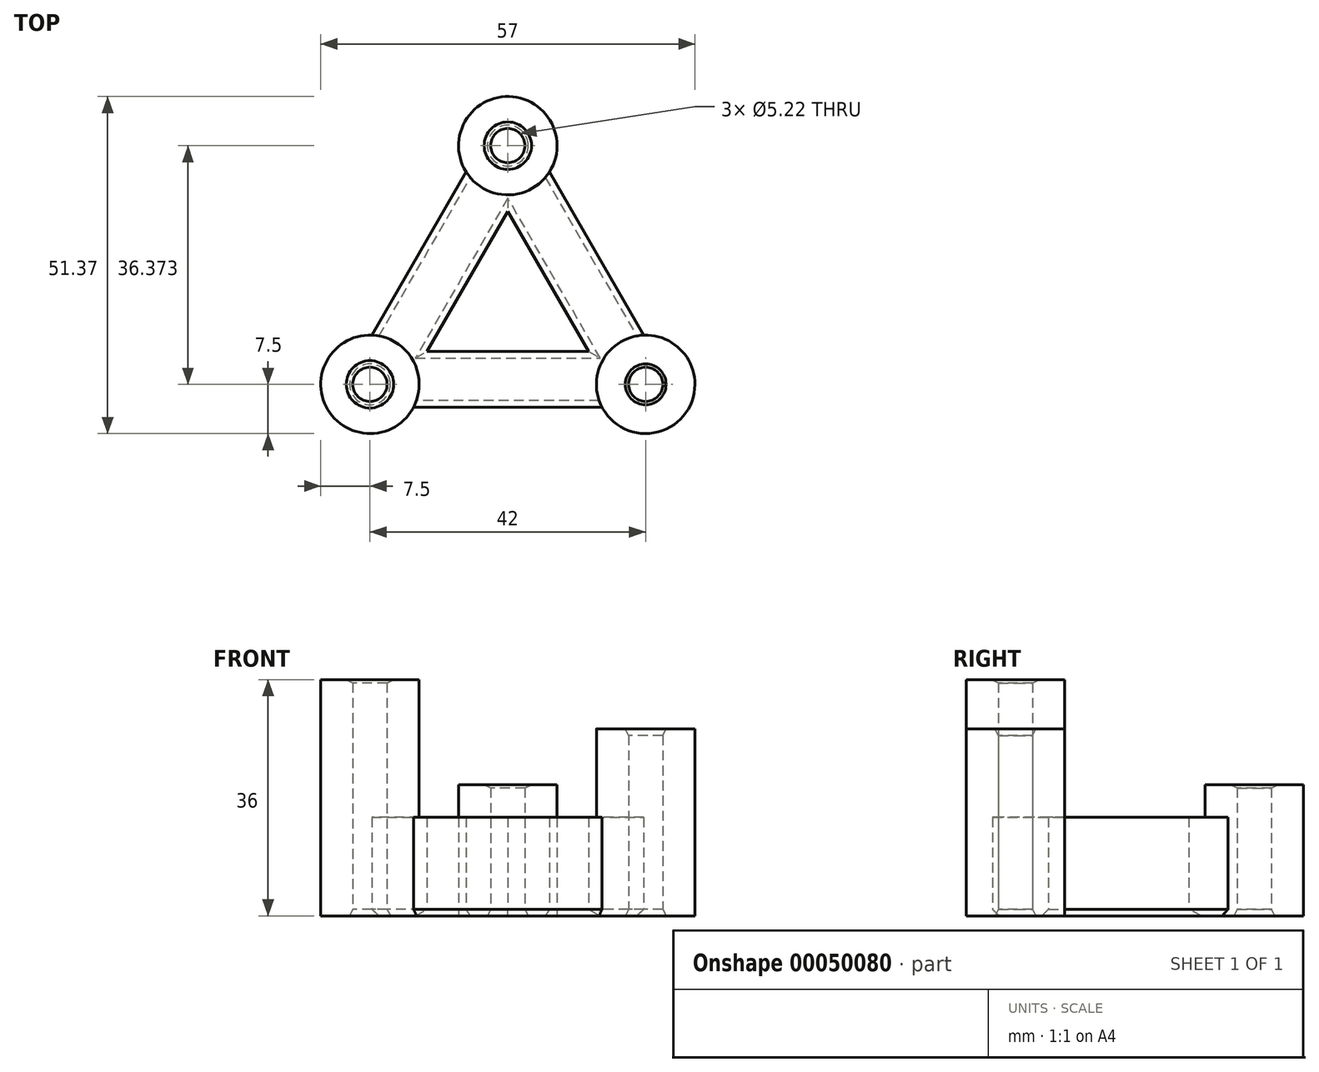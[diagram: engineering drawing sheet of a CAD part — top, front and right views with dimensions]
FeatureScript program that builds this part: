
annotation { "Feature Type Name" : "Feature", "Feature Type Description" : "" }
export const myFeature = defineFeature(function(context is Context, id is Id, definition is map)
    precondition{}
    {
        {
            var Q0;
            Q0=qCreatedBy(makeId("Top.planeOp"),FACE);
            var sketch = newSketch(context, id + "F0", { "sketchPlane" : qUnion([Q0])});
            skLineSegment(sketch, "E0", {"start": v(-21, 0) * mm, "end": v(21, 0) * mm, "construction": true});
            skLineSegment(sketch, "E1", {"start": v(21, 0) * mm, "end": v(0, 36.37) * mm, "construction": true});
            skLineSegment(sketch, "E2", {"start": v(0, 36.37) * mm, "end": v(-21, 0) * mm, "construction": true});
            skArc(sketch, "E3", {"start": v(6.35, 32.38) * mm, "mid": v(0, 43.87) * mm, "end": v(-6.35, 32.38) * mm});
            skArc(sketch, "E4", {"start": v(-20.71, 7.5) * mm, "mid": v(-27.5, -3.75) * mm, "end": v(-14.37, -3.5) * mm});
            skArc(sketch, "E5", {"start": v(14.37, -3.5) * mm, "mid": v(27.5, -3.75) * mm, "end": v(20.71, 7.5) * mm});
            skCircle(sketch, "E6", {"center": v(0, 36.37) * mm, "radius": 2.6 * mm});
            skCircle(sketch, "E7", {"center": v(21, 0) * mm, "radius": 2.6 * mm});
            skCircle(sketch, "E8", {"center": v(-21, 0) * mm, "radius": 2.6 * mm});
            skLineSegment(sketch, "E9", {"start": v(-20.71, 7.5) * mm, "end": v(-6.35, 32.38) * mm});
            skLineSegment(sketch, "E10", {"start": v(6.35, 32.38) * mm, "end": v(20.71, 7.5) * mm});
            skLineSegment(sketch, "E11", {"start": v(14.37, -3.5) * mm, "end": v(-14.37, -3.5) * mm});
            skLineSegment(sketch, "E12", {"start": v(-12.34, 5) * mm, "end": v(12.34, 5) * mm});
            skLineSegment(sketch, "E13", {"start": v(12.34, 5) * mm, "end": v(0, 26.37) * mm});
            skLineSegment(sketch, "E14", {"start": v(0, 26.37) * mm, "end": v(-12.34, 5) * mm});
            skSolve(sketch);
        }
        {
            var Q0;
            Q0=makeQuery(id+"F0.imprint","IMPRINT",FACE,{"disambiguationData":[TD([[makeQuery(id+"F0.imprint","IMPRINT",EDGE,{"derivedFrom":sQuery(id+"F0.wireOp",EDGE,"E3")}),1.0]])]});
            extrude(context, id + "F1", {"entities" : qUnion([Q0]), "depth" : 15 * mm, "offsetDistance" : 25 * mm});
        }
        {
            var Q0;
            Q0=makeQuery(id+"F1.opExtrude","CAP_FACE",FACE,{"disambiguationData":[OSD([sQuery(id+"F0.wireOp",EDGE,"E3"),sQuery(id+"F0.wireOp",EDGE,"E4"),sQuery(id+"F0.wireOp",EDGE,"E5"),sQuery(id+"F0.wireOp",EDGE,"E6"),sQuery(id+"F0.wireOp",EDGE,"E7"),sQuery(id+"F0.wireOp",EDGE,"E8"),sQuery(id+"F0.wireOp",EDGE,"E9"),sQuery(id+"F0.wireOp",EDGE,"E10"),sQuery(id+"F0.wireOp",EDGE,"E11"),sQuery(id+"F0.wireOp",EDGE,"c4641964-dd4c-461c-b4a4-2b9d8f9314cd"),sQuery(id+"F0.wireOp",EDGE,"2b7130c4-70b8-47ad-86bb-4bdc188b0346"),sQuery(id+"F0.wireOp",EDGE,"b70aad69-238b-43fd-8bed-80073a28fd59")])],"isStart":false});
            var sketch = newSketch(context, id + "F2", { "sketchPlane" : qUnion([Q0])});
            skCircle(sketch, "E15.0", {"center": v(0, 36.37) * mm, "radius": 2.6 * mm});
            skArc(sketch, "E16.0", {"start": v(6.35, 32.38) * mm, "mid": v(0, 43.87) * mm, "end": v(-6.35, 32.38) * mm, "construction": true});
            skCircle(sketch, "E17", {"center": v(0, 36.37) * mm, "radius": 7.5 * mm});
            skSolve(sketch);
        }
        {
            var Q0;
            Q0 = qSketchRegion(id + "F2", true);
            extrude(context, id + "F3", {"entities" : qUnion([Q0]), "operationType" : NewBodyOperationType.ADD, "depth" : 5 * mm, "offsetDistance" : 25 * mm});
        }
        {
            var Q0;
            Q0=makeQuery(id+"F1.opExtrude","CAP_FACE",FACE,{"disambiguationData":[OSD([sQuery(id+"F0.wireOp",EDGE,"E3"),sQuery(id+"F0.wireOp",EDGE,"E4"),sQuery(id+"F0.wireOp",EDGE,"E5"),sQuery(id+"F0.wireOp",EDGE,"E6"),sQuery(id+"F0.wireOp",EDGE,"E7"),sQuery(id+"F0.wireOp",EDGE,"E8"),sQuery(id+"F0.wireOp",EDGE,"E9"),sQuery(id+"F0.wireOp",EDGE,"E10"),sQuery(id+"F0.wireOp",EDGE,"E11"),sQuery(id+"F0.wireOp",EDGE,"c4641964-dd4c-461c-b4a4-2b9d8f9314cd"),sQuery(id+"F0.wireOp",EDGE,"2b7130c4-70b8-47ad-86bb-4bdc188b0346"),sQuery(id+"F0.wireOp",EDGE,"b70aad69-238b-43fd-8bed-80073a28fd59")])],"isStart":false});
            var sketch = newSketch(context, id + "F4", { "sketchPlane" : qUnion([Q0])});
            skCircle(sketch, "E18.0", {"center": v(21, 0) * mm, "radius": 2.61 * mm});
            skArc(sketch, "E19.0", {"start": v(14.37, -3.5) * mm, "mid": v(27.5, -3.75) * mm, "end": v(20.71, 7.5) * mm, "construction": true});
            skCircle(sketch, "E20", {"center": v(21, 0) * mm, "radius": 7.5 * mm});
            skSolve(sketch);
        }
        {
            var Q0;
            Q0 = qSketchRegion(id + "F4", true);
            extrude(context, id + "F5", {"entities" : qUnion([Q0]), "operationType" : NewBodyOperationType.ADD, "depth" : 13.5 * mm, "offsetDistance" : 25 * mm});
        }
        {
            var Q0;
            {var subQ0=sQuery(id+"F0.wireOp",EDGE,"2b7130c4-70b8-47ad-86bb-4bdc188b0346");var subQ1=sQuery(id+"F0.wireOp",EDGE,"c4641964-dd4c-461c-b4a4-2b9d8f9314cd");var subQ2=sQuery(id+"F0.wireOp",EDGE,"E9");var subQ3=sQuery(id+"F0.wireOp",EDGE,"E8");var subQ4=sQuery(id+"F0.wireOp",EDGE,"E3");var subQ5=sQuery(id+"F0.wireOp",EDGE,"b70aad69-238b-43fd-8bed-80073a28fd59");var subQ6=sQuery(id+"F0.wireOp",EDGE,"E11");var subQ7=sQuery(id+"F0.wireOp",EDGE,"E5");var subQ8=sQuery(id+"F0.wireOp",EDGE,"E4");var subQ9=makeQuery(id+"F1.opExtrude","CAP_FACE",FACE,{"disambiguationData":[OSD([subQ4,subQ8,subQ7,sQuery(id+"F0.wireOp",EDGE,"E6"),sQuery(id+"F0.wireOp",EDGE,"E7"),subQ3,subQ2,sQuery(id+"F0.wireOp",EDGE,"E10"),subQ6,subQ1,subQ0,subQ5])],"isStart":false});Q0=makeQuery(id+"F5.boolean.opBoolean","SPLIT",FACE,{"disambiguationData":[TD([makeQuery(id+"F1.opExtrude","SWEPT_FACE",FACE,{"disambiguationData":[OSD([subQ8])]})])],"derivedFrom":subQ9});}
            var sketch = newSketch(context, id + "F6", { "sketchPlane" : qUnion([Q0])});
            skCircle(sketch, "E21.0", {"center": v(-21, 0) * mm, "radius": 2.61 * mm});
            skArc(sketch, "E22.0", {"start": v(-20.71, 7.5) * mm, "mid": v(-27.5, -3.75) * mm, "end": v(-14.37, -3.5) * mm, "construction": true});
            skCircle(sketch, "E23", {"center": v(-21, 0) * mm, "radius": 7.5 * mm});
            skSolve(sketch);
        }
        {
            var Q0;
            Q0 = qSketchRegion(id + "F6", true);
            extrude(context, id + "F7", {"entities" : qUnion([Q0]), "operationType" : NewBodyOperationType.ADD, "depth" : 21 * mm});
        }
        {
            var Q0;
            Q0=makeQuery(id+"F1.opExtrude","CAP_EDGE",EDGE,{"disambiguationData":[OSD([sQuery(id+"F0.wireOp",EDGE,"E7")])],"isStart":true});
            var Q1;
            Q1=makeQuery(id+"F1.opExtrude","CAP_EDGE",EDGE,{"disambiguationData":[OSD([sQuery(id+"F0.wireOp",EDGE,"E6")])],"isStart":true});
            var Q2;
            Q2=makeQuery(id+"F1.opExtrude","CAP_EDGE",EDGE,{"disambiguationData":[OSD([sQuery(id+"F0.wireOp",EDGE,"E8")])],"isStart":true});
            var Q3;
            Q3=makeQuery(id+"F5.opExtrude","CAP_EDGE",EDGE,{"disambiguationData":[OSD([sQuery(id+"F4.wireOp",EDGE,"E18.0")])],"isStart":false});
            var Q4;
            Q4=makeQuery(id+"F3.opExtrude","CAP_EDGE",EDGE,{"disambiguationData":[OSD([sQuery(id+"F2.wireOp",EDGE,"E15.0")])],"isStart":false});
            var Q5;
            Q5=makeQuery(id+"F7.opExtrude","CAP_EDGE",EDGE,{"disambiguationData":[OSD([sQuery(id+"F6.wireOp",EDGE,"E21.0")])],"isStart":false});
            chamfer(context, id + "F8", {"entities" : qUnion([Q0, Q1, Q2, Q3, Q4, Q5]), "chamferType" : ChamferType.TWO_OFFSETS, "width1" : 0.5 * mm, "oppositeDirection" : false, "width2" : 1 * mm, "tangentPropagation" : true});
        }
        {
            var Q0;
            Q0=makeQuery(id+"F1.opExtrude","CAP_EDGE",EDGE,{"disambiguationData":[OSD([sQuery(id+"F0.wireOp",EDGE,"E13")])],"isStart":true});
            var Q1;
            Q1=makeQuery(id+"F1.opExtrude","CAP_EDGE",EDGE,{"disambiguationData":[OSD([sQuery(id+"F0.wireOp",EDGE,"E12")])],"isStart":true});
            var Q2;
            Q2=makeQuery(id+"F1.opExtrude","CAP_EDGE",EDGE,{"disambiguationData":[OSD([sQuery(id+"F0.wireOp",EDGE,"E14")])],"isStart":true});
            var Q3;
            Q3=makeQuery(id+"F1.opExtrude","CAP_EDGE",EDGE,{"disambiguationData":[OSD([sQuery(id+"F0.wireOp",EDGE,"E11")])],"isStart":true});
            var Q4;
            Q4=makeQuery(id+"F1.opExtrude","CAP_EDGE",EDGE,{"disambiguationData":[OSD([sQuery(id+"F0.wireOp",EDGE,"E9")])],"isStart":true});
            var Q5;
            Q5=makeQuery(id+"F1.opExtrude","CAP_EDGE",EDGE,{"disambiguationData":[OSD([sQuery(id+"F0.wireOp",EDGE,"E10")])],"isStart":true});
            chamfer(context, id + "F9", {"entities" : qUnion([Q0, Q1, Q2, Q3, Q4, Q5]), "width" : 1 * mm, "tangentPropagation" : true});
        }
    });
